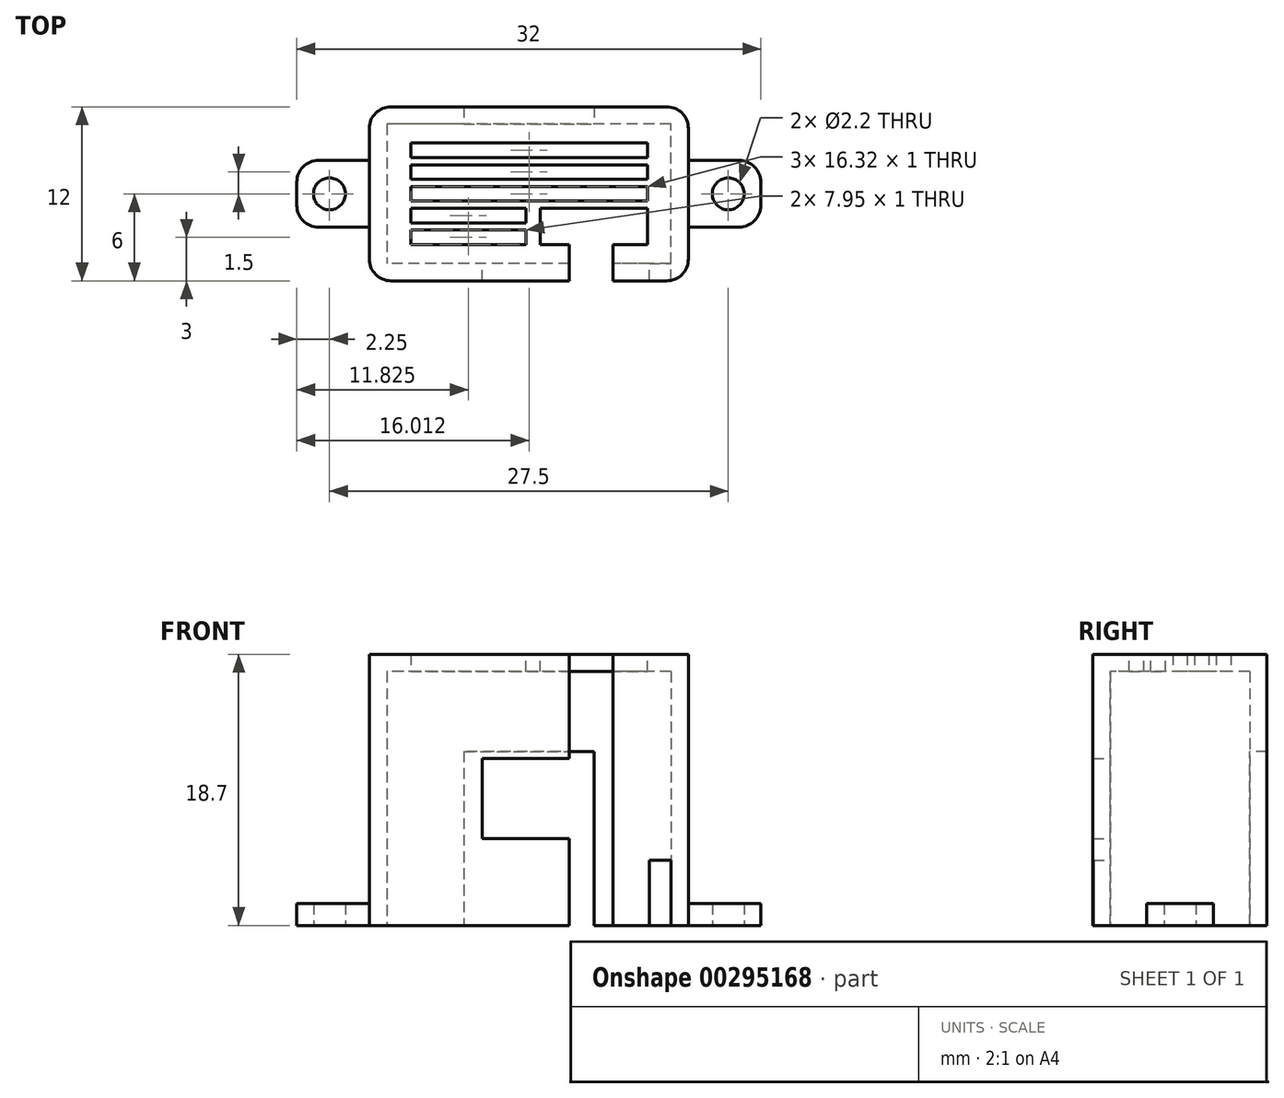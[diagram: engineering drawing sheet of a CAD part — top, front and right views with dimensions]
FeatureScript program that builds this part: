
annotation { "Feature Type Name" : "Feature", "Feature Type Description" : "" }
export const myFeature = defineFeature(function(context is Context, id is Id, definition is map)
    precondition{}
    {
        {
            var Q0;
            Q0=qCreatedBy(makeId("Top.planeOp"),FACE);
            var sketch = newSketch(context, id + "F0", { "sketchPlane" : qUnion([Q0])});
            skLineSegment(sketch, "E0.bottom", {"start": v(1.5, 0) * mm, "end": v(20.5, 0) * mm});
            skLineSegment(sketch, "E0.top", {"start": v(1.5, -12) * mm, "end": v(20.5, -12) * mm});
            skLineSegment(sketch, "E0.left", {"start": v(0, -1.5) * mm, "end": v(0, -10.5) * mm});
            skLineSegment(sketch, "E0.right", {"start": v(22, -1.5) * mm, "end": v(22, -10.5) * mm});
            skLineSegment(sketch, "E1.bottom", {"start": v(0, -3.7) * mm, "end": v(-3.5, -3.7) * mm});
            skLineSegment(sketch, "E1.top", {"start": v(0, -8.3) * mm, "end": v(-3.5, -8.3) * mm});
            skLineSegment(sketch, "E1.left", {"start": v(0, -3.7) * mm, "end": v(0, -8.3) * mm});
            skLineSegment(sketch, "E1.right", {"start": v(-5, -5.2) * mm, "end": v(-5, -6.8) * mm});
            skLineSegment(sketch, "E2.bottom", {"start": v(22, -3.7) * mm, "end": v(25.5, -3.7) * mm});
            skLineSegment(sketch, "E2.top", {"start": v(22, -8.3) * mm, "end": v(25.5, -8.3) * mm});
            skLineSegment(sketch, "E2.left", {"start": v(22, -3.7) * mm, "end": v(22, -8.3) * mm});
            skLineSegment(sketch, "E2.right", {"start": v(27, -5.2) * mm, "end": v(27, -6.8) * mm});
            skLineSegment(sketch, "E3", {"start": v(5.98, -6) * mm, "end": v(14.86, -6) * mm, "construction": true});
            skPoint(sketch, "E3.startSnap0", {"position": v(0, -6) * mm});
            skCircle(sketch, "E4", {"center": v(-2.75, -6) * mm, "radius": 1.1 * mm});
            skCircle(sketch, "E5", {"center": v(24.75, -6) * mm, "radius": 1.1 * mm});
            skPoint(sketch, "E6.visualSharp", {"position": v(-5, -3.7) * mm});
            skArc(sketch, "E7.filletArc", {"start": v(-3.5, -3.7) * mm, "mid": v(-4.56, -4.14) * mm, "end": v(-5, -5.2) * mm});
            skPoint(sketch, "E8.visualSharp", {"position": v(-5, -8.3) * mm});
            skArc(sketch, "E8.filletArc", {"start": v(-5, -6.8) * mm, "mid": v(-4.56, -7.86) * mm, "end": v(-3.5, -8.3) * mm});
            skPoint(sketch, "E9.visualSharp", {"position": v(27, -3.7) * mm});
            skArc(sketch, "E9.filletArc", {"start": v(27, -5.2) * mm, "mid": v(26.56, -4.14) * mm, "end": v(25.5, -3.7) * mm});
            skPoint(sketch, "E10.visualSharp", {"position": v(27, -8.3) * mm});
            skArc(sketch, "E10.filletArc", {"start": v(25.5, -8.3) * mm, "mid": v(26.56, -7.86) * mm, "end": v(27, -6.8) * mm});
            skPoint(sketch, "E11.visualSharp", {"position": v(0, 0) * mm});
            skArc(sketch, "E11.filletArc", {"start": v(1.5, 0) * mm, "mid": v(0.44, -0.44) * mm, "end": v(0, -1.5) * mm});
            skPoint(sketch, "E12.visualSharp", {"position": v(22, 0) * mm});
            skArc(sketch, "E12.filletArc", {"start": v(22, -1.5) * mm, "mid": v(21.56, -0.44) * mm, "end": v(20.5, 0) * mm});
            skPoint(sketch, "E13.visualSharp", {"position": v(22, -12) * mm});
            skArc(sketch, "E13.filletArc", {"start": v(20.5, -12) * mm, "mid": v(21.56, -11.56) * mm, "end": v(22, -10.5) * mm});
            skPoint(sketch, "E14.visualSharp", {"position": v(0, -12) * mm});
            skArc(sketch, "E14.filletArc", {"start": v(0, -10.5) * mm, "mid": v(0.44, -11.56) * mm, "end": v(1.5, -12) * mm});
            skLineSegment(sketch, "E15.0", {"start": v(20.8, -1.5) * mm, "end": v(20.8, -10.5) * mm});
            skLineSegment(sketch, "E15.2", {"start": v(1.5, -1.2) * mm, "end": v(20.5, -1.2) * mm});
            skLineSegment(sketch, "E15.3", {"start": v(1.5, -10.8) * mm, "end": v(20.5, -10.8) * mm});
            skLineSegment(sketch, "E15.5", {"start": v(1.2, -1.5) * mm, "end": v(1.2, -10.5) * mm});
            skLineSegment(sketch, "E16", {"start": v(20.8, -10.5) * mm, "end": v(20.8, -10.8) * mm});
            skLineSegment(sketch, "E17", {"start": v(20.8, -10.8) * mm, "end": v(20.5, -10.8) * mm});
            skLineSegment(sketch, "E18", {"start": v(20.8, -1.5) * mm, "end": v(20.8, -1.2) * mm});
            skLineSegment(sketch, "E19", {"start": v(20.8, -1.2) * mm, "end": v(20.5, -1.2) * mm});
            skLineSegment(sketch, "E20", {"start": v(1.5, -1.2) * mm, "end": v(1.2, -1.2) * mm});
            skLineSegment(sketch, "E21", {"start": v(1.2, -1.2) * mm, "end": v(1.2, -1.5) * mm});
            skLineSegment(sketch, "E22", {"start": v(1.2, -10.5) * mm, "end": v(1.2, -10.8) * mm});
            skLineSegment(sketch, "E23", {"start": v(1.2, -10.8) * mm, "end": v(1.5, -10.8) * mm});
            skSolve(sketch);
        }
        {
            var Q0;
            Q0=makeQuery(id+"F0.imprint","IMPRINT",FACE,{"disambiguationData":[TD([[makeQuery(id+"F0.imprint","IMPRINT",EDGE,{"derivedFrom":sQuery(id+"F0.wireOp",EDGE,"E0.bottom")}),-1.0]])]});
            var Q1;
            Q1=makeQuery(id+"F0.imprint","IMPRINT",FACE,{"disambiguationData":[TD([[makeQuery(id+"F0.imprint","IMPRINT",EDGE,{"derivedFrom":sQuery(id+"F0.wireOp",EDGE,"E1.bottom")}),1.0]])]});
            var Q2;
            Q2=makeQuery(id+"F0.imprint","IMPRINT",FACE,{"disambiguationData":[TD([[makeQuery(id+"F0.imprint","IMPRINT",EDGE,{"derivedFrom":sQuery(id+"F0.wireOp",EDGE,"E2.bottom")}),-1.0]])]});
            var Q3;
            {var subQ0=sQuery(id+"F0.wireOp",EDGE,"jaEvkIbK-e3yD-Nrfl-q2IN-t7q462HMhGoy");Q3=makeQuery(id+"F0.imprint","IMPRINT",FACE,{"disambiguationData":[TD([[makeQuery(id+"F0.imprint","IMPRINT",EDGE,{"derivedFrom":subQ0}),1.0]])]});}
            extrude(context, id + "F1", {"entities" : qUnion([Q0, Q1, Q2, Q3]), "depth" : 1.5 * mm});
        }
        {
            var Q0;
            Q0=makeQuery(id+"F1.opExtrude","CAP_FACE",FACE,{"disambiguationData":[OSD([sQuery(id+"F0.wireOp",EDGE,"E0.bottom"),sQuery(id+"F0.wireOp",EDGE,"E0.top"),sQuery(id+"F0.wireOp",EDGE,"E0.left"),sQuery(id+"F0.wireOp",EDGE,"E0.right"),sQuery(id+"F0.wireOp",EDGE,"E1.bottom"),sQuery(id+"F0.wireOp",EDGE,"E1.top"),sQuery(id+"F0.wireOp",EDGE,"E1.right"),sQuery(id+"F0.wireOp",EDGE,"E2.bottom"),sQuery(id+"F0.wireOp",EDGE,"E2.top"),sQuery(id+"F0.wireOp",EDGE,"E2.right"),sQuery(id+"F0.wireOp",EDGE,"E4"),sQuery(id+"F0.wireOp",EDGE,"E5"),sQuery(id+"F0.wireOp",EDGE,"E7.filletArc"),sQuery(id+"F0.wireOp",EDGE,"E8.filletArc"),sQuery(id+"F0.wireOp",EDGE,"E9.filletArc"),sQuery(id+"F0.wireOp",EDGE,"E10.filletArc"),sQuery(id+"F0.wireOp",EDGE,"E11.filletArc"),sQuery(id+"F0.wireOp",EDGE,"E12.filletArc"),sQuery(id+"F0.wireOp",EDGE,"E13.filletArc"),sQuery(id+"F0.wireOp",EDGE,"E14.filletArc"),sQuery(id+"F0.wireOp",EDGE,"E15.0"),sQuery(id+"F0.wireOp",EDGE,"E15.2"),sQuery(id+"F0.wireOp",EDGE,"E15.3"),sQuery(id+"F0.wireOp",EDGE,"E15.5"),sQuery(id+"F0.wireOp",EDGE,"E16"),sQuery(id+"F0.wireOp",EDGE,"E17"),sQuery(id+"F0.wireOp",EDGE,"E18"),sQuery(id+"F0.wireOp",EDGE,"E19"),sQuery(id+"F0.wireOp",EDGE,"E20"),sQuery(id+"F0.wireOp",EDGE,"E21"),sQuery(id+"F0.wireOp",EDGE,"E22"),sQuery(id+"F0.wireOp",EDGE,"E23")])],"isStart":false});
            var sketch = newSketch(context, id + "F2", { "sketchPlane" : qUnion([Q0])});
            skLineSegment(sketch, "E24", {"start": v(22, -8.3) * mm, "end": v(22, -3.7) * mm});
            skLineSegment(sketch, "E25", {"start": v(0, -8.3) * mm, "end": v(0, -3.7) * mm});
            skSolve(sketch);
        }
        {
            var Q0;
            Q0=makeQuery(id+"F2.imprint","IMPRINT",FACE,{"disambiguationData":[TD([[makeQuery(id+"F2.imprint","IMPRINT",EDGE,{"derivedFrom":sQuery(id+"F2.wireOp",EDGE,"E24")}),1.0]])]});
            extrude(context, id + "F3", {"entities" : qUnion([Q0]), "operationType" : NewBodyOperationType.ADD, "depth" : 16 * mm});
        }
        {
            var Q0;
            {var subQ0=sQuery(id+"F0.wireOp",EDGE,"E23");var subQ1=sQuery(id+"F0.wireOp",EDGE,"E17");var subQ2=sQuery(id+"F0.wireOp",EDGE,"E15.3");Q0=makeQuery(id+"F3.boolean.opBoolean","MERGE",FACE,{"derivedFrom":[makeQuery(id+"F1.opExtrude","SWEPT_FACE",FACE,{"disambiguationData":[OSD([subQ2,subQ1,subQ0])]}),makeQuery(id+"F3.opExtrude","SWEPT_FACE",FACE,{"disambiguationData":[OSD([subQ2,subQ1,subQ0])]})]});}
            var sketch = newSketch(context, id + "F4", { "sketchPlane" : qUnion([Q0])});
            skLineSegment(sketch, "E26", {"start": v(-16.8, 0) * mm, "end": v(-16.8, 17.5) * mm});
            skLineSegment(sketch, "E27", {"start": v(-16.8, 17.5) * mm, "end": v(-13.8, 17.5) * mm});
            skLineSegment(sketch, "E28", {"start": v(-13.8, 17.5) * mm, "end": v(-13.8, 0) * mm});
            skLineSegment(sketch, "E29", {"start": v(-19.3, 0) * mm, "end": v(-19.3, 4.5) * mm});
            skLineSegment(sketch, "E30", {"start": v(-19.3, 4.5) * mm, "end": v(-20.8, 4.5) * mm});
            skLineSegment(sketch, "E31.bottom", {"start": v(-13.8, 6) * mm, "end": v(-7.8, 6) * mm});
            skLineSegment(sketch, "E31.top", {"start": v(-13.8, 11.5) * mm, "end": v(-7.8, 11.5) * mm});
            skLineSegment(sketch, "E31.left", {"start": v(-13.8, 6) * mm, "end": v(-13.8, 11.5) * mm});
            skLineSegment(sketch, "E31.right", {"start": v(-7.8, 6) * mm, "end": v(-7.8, 11.5) * mm});
            skSolve(sketch);
        }
        {
            var Q0;
            {var subQ0=sQuery(id+"F4.wireOp",EDGE,"E29");Q0=makeQuery(id+"F4.imprint","IMPRINT",FACE,{"disambiguationData":[TD([[makeQuery(id+"F4.imprint","IMPRINT",EDGE,{"derivedFrom":subQ0}),1.0]])]});}
            var Q1;
            {var subQ0=sQuery(id+"F4.wireOp",EDGE,"E26");Q1=makeQuery(id+"F4.imprint","IMPRINT",FACE,{"disambiguationData":[TD([[makeQuery(id+"F4.imprint","IMPRINT",EDGE,{"derivedFrom":subQ0}),-1.0]])]});}
            var Q2;
            Q2=makeQuery(id+"F4.imprint","IMPRINT",FACE,{"disambiguationData":[TD([[makeQuery(id+"F4.imprint","IMPRINT",EDGE,{"derivedFrom":sQuery(id+"F4.wireOp",EDGE,"E31.bottom")}),1.0]])]});
            extrude(context, id + "F5", {"entities" : qUnion([Q0, Q1, Q2]), "operationType" : NewBodyOperationType.REMOVE, "oppositeDirection" : true, "depth" : 1.2 * mm});
        }
        {
            var Q0;
            {var subQ0=sQuery(id+"F0.wireOp",EDGE,"E20");var subQ1=sQuery(id+"F0.wireOp",EDGE,"E19");var subQ2=sQuery(id+"F0.wireOp",EDGE,"E15.2");Q0=makeQuery(id+"F3.boolean.opBoolean","MERGE",FACE,{"derivedFrom":[makeQuery(id+"F1.opExtrude","SWEPT_FACE",FACE,{"disambiguationData":[OSD([subQ2,subQ1,subQ0])]}),makeQuery(id+"F3.opExtrude","SWEPT_FACE",FACE,{"disambiguationData":[OSD([subQ2,subQ1,subQ0])]})]});}
            var sketch = newSketch(context, id + "F6", { "sketchPlane" : qUnion([Q0])});
            skLineSegment(sketch, "E32.bottom", {"start": v(6.5, 0) * mm, "end": v(15.5, 0) * mm});
            skLineSegment(sketch, "E32.top", {"start": v(6.5, 12) * mm, "end": v(15.5, 12) * mm});
            skLineSegment(sketch, "E32.left", {"start": v(6.5, 0) * mm, "end": v(6.5, 12) * mm});
            skLineSegment(sketch, "E32.right", {"start": v(15.5, 0) * mm, "end": v(15.5, 12) * mm});
            skSolve(sketch);
        }
        {
            var Q0;
            Q0=makeQuery(id+"F6.imprint","IMPRINT",FACE,{"disambiguationData":[TD([[makeQuery(id+"F6.imprint","IMPRINT",EDGE,{"derivedFrom":sQuery(id+"F6.wireOp",EDGE,"E32.bottom")}),-1.0]])]});
            extrude(context, id + "F7", {"entities" : qUnion([Q0]), "operationType" : NewBodyOperationType.REMOVE, "oppositeDirection" : true, "depth" : 25 * mm});
        }
        {
            var Q0;
            Q0=makeQuery(id+"F3.opExtrude","CAP_FACE",FACE,{"disambiguationData":[OSD([sQuery(id+"F0.wireOp",EDGE,"E0.bottom"),sQuery(id+"F0.wireOp",EDGE,"E0.top"),sQuery(id+"F0.wireOp",EDGE,"E0.left"),sQuery(id+"F0.wireOp",EDGE,"E0.right"),sQuery(id+"F0.wireOp",EDGE,"E11.filletArc"),sQuery(id+"F0.wireOp",EDGE,"E12.filletArc"),sQuery(id+"F0.wireOp",EDGE,"E13.filletArc"),sQuery(id+"F0.wireOp",EDGE,"E14.filletArc"),sQuery(id+"F0.wireOp",EDGE,"E15.0"),sQuery(id+"F0.wireOp",EDGE,"E15.2"),sQuery(id+"F0.wireOp",EDGE,"E15.3"),sQuery(id+"F0.wireOp",EDGE,"E15.5"),sQuery(id+"F0.wireOp",EDGE,"E16"),sQuery(id+"F0.wireOp",EDGE,"E17"),sQuery(id+"F0.wireOp",EDGE,"E18"),sQuery(id+"F0.wireOp",EDGE,"E19"),sQuery(id+"F0.wireOp",EDGE,"E20"),sQuery(id+"F0.wireOp",EDGE,"E21"),sQuery(id+"F0.wireOp",EDGE,"E22"),sQuery(id+"F0.wireOp",EDGE,"E23"),sQuery(id+"F2.wireOp",EDGE,"E24"),sQuery(id+"F2.wireOp",EDGE,"E25")])],"isStart":false});
            var sketch = newSketch(context, id + "F8", { "sketchPlane" : qUnion([Q0])});
            skLineSegment(sketch, "E33", {"start": v(16.8, -12) * mm, "end": v(13.8, -12) * mm});
            skLineSegment(sketch, "E34", {"start": v(4.97, -6) * mm, "end": v(16.54, -6) * mm, "construction": true});
            skPoint(sketch, "E34.startSnap0", {"position": v(1.2, -6) * mm});
            skLineSegment(sketch, "E35.bottom", {"start": v(2.85, -2.5) * mm, "end": v(19.17, -2.5) * mm});
            skLineSegment(sketch, "E35.top", {"start": v(2.85, -3.5) * mm, "end": v(19.17, -3.5) * mm});
            skLineSegment(sketch, "E35.left", {"start": v(2.85, -2.5) * mm, "end": v(2.85, -3.5) * mm});
            skLineSegment(sketch, "E35.right", {"start": v(19.17, -2.5) * mm, "end": v(19.17, -3.5) * mm});
            skLineSegment(sketch, "E36.bottom", {"start": v(2.85, -4) * mm, "end": v(19.17, -4) * mm});
            skLineSegment(sketch, "E36.top", {"start": v(2.85, -5) * mm, "end": v(19.17, -5) * mm});
            skLineSegment(sketch, "E36.left", {"start": v(2.85, -4) * mm, "end": v(2.85, -5) * mm});
            skLineSegment(sketch, "E36.right", {"start": v(19.17, -4) * mm, "end": v(19.17, -5) * mm});
            skPoint(sketch, "E37.firstSnap0", {"position": v(2.85, -4.5) * mm});
            skLineSegment(sketch, "E37.bottom", {"start": v(2.85, -5.5) * mm, "end": v(19.17, -5.5) * mm});
            skLineSegment(sketch, "E37.top", {"start": v(2.85, -6.5) * mm, "end": v(19.17, -6.5) * mm});
            skLineSegment(sketch, "E37.left", {"start": v(2.85, -5.5) * mm, "end": v(2.85, -6.5) * mm});
            skLineSegment(sketch, "E37.right", {"start": v(19.17, -5.5) * mm, "end": v(19.17, -6.5) * mm});
            skLineSegment(sketch, "E38.MirrorCS", {"start": v(2.85, -7) * mm, "end": v(19.17, -7) * mm});
            skLineSegment(sketch, "E39.MirrorCS", {"start": v(2.85, -9.5) * mm, "end": v(2.85, -8.5) * mm});
            skLineSegment(sketch, "E40.MirrorCS", {"start": v(2.85, -9.5) * mm, "end": v(19.17, -9.5) * mm});
            skLineSegment(sketch, "E41.MirrorCS", {"start": v(2.85, -8) * mm, "end": v(19.17, -8) * mm});
            skLineSegment(sketch, "E42.MirrorCS", {"start": v(19.17, -8) * mm, "end": v(19.17, -7) * mm});
            skPoint(sketch, "E43.MirrorP", {"position": v(2.85, -7.5) * mm});
            skLineSegment(sketch, "E44.MirrorCS", {"start": v(2.85, -8.5) * mm, "end": v(19.17, -8.5) * mm});
            skLineSegment(sketch, "E45.MirrorCS", {"start": v(2.85, -8) * mm, "end": v(2.85, -7) * mm});
            skLineSegment(sketch, "E46.MirrorCS", {"start": v(19.17, -9.5) * mm, "end": v(19.17, -8.5) * mm});
            skSolve(sketch);
        }
        {
            var Q0;
            {var subQ16=sQuery(id+"F0.wireOp",EDGE,"E0.bottom");Q0=makeQuery(id+"F8.imprint","IMPRINT",FACE,{"disambiguationData":[TD([[makeQuery(id+"F8.imprint","IMPRINT",EDGE,{"derivedFrom":makeQuery(id+"F3.opExtrude","CAP_EDGE",EDGE,{"disambiguationData":[OSD([subQ16])],"isStart":false})}),-1.0]])]});}
            var Q1;
            Q1=makeQuery(id+"F8.imprint","IMPRINT",FACE,{"disambiguationData":[TD([[makeQuery(id+"F8.imprint","IMPRINT",EDGE,{"derivedFrom":sQuery(id+"F8.wireOp",EDGE,"E33")}),-1.0]])]});
            extrude(context, id + "F9", {"entities" : qUnion([Q0, Q1]), "operationType" : NewBodyOperationType.ADD, "depth" : 1.2 * mm});
        }
        {
            var Q0;
            {var subQ0=sQuery(id+"F0.wireOp",EDGE,"E0.top");var subQ13=sQuery(id+"F0.wireOp",EDGE,"E14.filletArc");var subQ14=sQuery(id+"F0.wireOp",EDGE,"E13.filletArc");var subQ22=makeQuery(id+"F3.boolean.opBoolean","MERGE",FACE,{"derivedFrom":[makeQuery(id+"F1.opExtrude","SWEPT_FACE",FACE,{"disambiguationData":[OSD([subQ0])]}),makeQuery(id+"F3.opExtrude","SWEPT_FACE",FACE,{"disambiguationData":[OSD([subQ0])]})]});Q0=makeQuery(id+"F9.boolean.opBoolean","MERGE",FACE,{"derivedFrom":[makeQuery(id+"F5.boolean.opBoolean","SPLIT",FACE,{"disambiguationData":[TD([makeQuery(id+"F1.opExtrude","SWEPT_FACE",FACE,{"disambiguationData":[OSD([subQ13])]})])],"derivedFrom":subQ22}),makeQuery(id+"F5.boolean.opBoolean","SPLIT",FACE,{"disambiguationData":[TD([makeQuery(id+"F1.opExtrude","SWEPT_FACE",FACE,{"disambiguationData":[OSD([subQ14])]})])],"derivedFrom":subQ22}),makeQuery(id+"F9.opExtrude","SWEPT_FACE",FACE,{"disambiguationData":[OSD([subQ0,sQuery(id+"F8.wireOp",EDGE,"E33")])]})]});}
            var sketch = newSketch(context, id + "F10", { "sketchPlane" : qUnion([Q0])});
            skLineSegment(sketch, "E47", {"start": v(13.8, 17.5) * mm, "end": v(13.8, 18.7) * mm});
            skLineSegment(sketch, "E48", {"start": v(16.8, 17.5) * mm, "end": v(16.8, 18.7) * mm});
            skSolve(sketch);
        }
        {
            var Q0;
            {var subQ0=sQuery(id+"F10.wireOp",EDGE,"E47");Q0=makeQuery(id+"F10.imprint","IMPRINT",FACE,{"disambiguationData":[TD([[makeQuery(id+"F10.imprint","IMPRINT",EDGE,{"derivedFrom":subQ0}),-1.0]])]});}
            extrude(context, id + "F11", {"entities" : qUnion([Q0]), "operationType" : NewBodyOperationType.REMOVE, "oppositeDirection" : true, "depth" : 4 * mm});
        }
        {
            var Q0;
            Q0=makeQuery(id+"F9.opExtrude","CAP_FACE",FACE,{"disambiguationData":[OSD([sQuery(id+"F0.wireOp",EDGE,"E0.bottom"),sQuery(id+"F0.wireOp",EDGE,"E0.top"),sQuery(id+"F0.wireOp",EDGE,"E0.left"),sQuery(id+"F0.wireOp",EDGE,"E0.right"),sQuery(id+"F0.wireOp",EDGE,"E11.filletArc"),sQuery(id+"F0.wireOp",EDGE,"E12.filletArc"),sQuery(id+"F0.wireOp",EDGE,"E13.filletArc"),sQuery(id+"F0.wireOp",EDGE,"E14.filletArc"),sQuery(id+"F2.wireOp",EDGE,"E24"),sQuery(id+"F2.wireOp",EDGE,"E25"),sQuery(id+"F8.wireOp",EDGE,"E33"),sQuery(id+"F8.wireOp",EDGE,"E35.bottom"),sQuery(id+"F8.wireOp",EDGE,"E35.top"),sQuery(id+"F8.wireOp",EDGE,"E35.left"),sQuery(id+"F8.wireOp",EDGE,"E35.right"),sQuery(id+"F8.wireOp",EDGE,"E36.bottom"),sQuery(id+"F8.wireOp",EDGE,"E36.top"),sQuery(id+"F8.wireOp",EDGE,"E36.left"),sQuery(id+"F8.wireOp",EDGE,"E36.right"),sQuery(id+"F8.wireOp",EDGE,"E37.bottom"),sQuery(id+"F8.wireOp",EDGE,"E37.top"),sQuery(id+"F8.wireOp",EDGE,"E37.left"),sQuery(id+"F8.wireOp",EDGE,"E37.right"),sQuery(id+"F8.wireOp",EDGE,"E38.MirrorCS"),sQuery(id+"F8.wireOp",EDGE,"E39.MirrorCS"),sQuery(id+"F8.wireOp",EDGE,"E40.MirrorCS"),sQuery(id+"F8.wireOp",EDGE,"E41.MirrorCS"),sQuery(id+"F8.wireOp",EDGE,"E42.MirrorCS"),sQuery(id+"F8.wireOp",EDGE,"E44.MirrorCS"),sQuery(id+"F8.wireOp",EDGE,"E45.MirrorCS"),sQuery(id+"F8.wireOp",EDGE,"E46.MirrorCS")])],"isStart":false});
            var sketch = newSketch(context, id + "F12", { "sketchPlane" : qUnion([Q0])});
            skLineSegment(sketch, "E49", {"start": v(13.8, -9.5) * mm, "end": v(13.8, -7) * mm});
            skLineSegment(sketch, "E50", {"start": v(10.8, -9.5) * mm, "end": v(10.8, -7) * mm});
            skLineSegment(sketch, "E51", {"start": v(16.8, -9.5) * mm, "end": v(16.8, -7) * mm});
            skLineSegment(sketch, "E52", {"start": v(19.17, -9.5) * mm, "end": v(19.17, -7) * mm});
            skSolve(sketch);
        }
        {
            var Q0;
            {var subQ2=sQuery(id+"F8.wireOp",EDGE,"E44.MirrorCS");var subQ4=sQuery(id+"F8.wireOp",EDGE,"E39.MirrorCS");var subQ10=makeQuery(id+"F9.opExtrude","SWEPT_FACE",FACE,{"disambiguationData":[OSD([subQ4])]});var subQ13=makeQuery(id+"F11.boolean.opBoolean","SPLIT",EDGE,{"disambiguationData":[TD([subQ10])],"derivedFrom":makeQuery(id+"F9.opExtrude","CAP_EDGE",EDGE,{"disambiguationData":[OSD([subQ2])],"isStart":false})});var subQ15=sQuery(id+"F12.wireOp",EDGE,"E50");var subQ17=makeQuery(id+"F12.imprint","INTERSECT",VERTEX,{"derivedFrom":[subQ13,subQ15]});Q0=makeQuery(id+"F12.imprint","IMPRINT",FACE,{"disambiguationData":[TD([[makeQuery(id+"F12.imprint","IMPRINT",EDGE,{"disambiguationData":[TD([[subQ17,1.0]])],"derivedFrom":subQ15}),-1.0]])]});}
            var Q1;
            {var subQ0=sQuery(id+"F12.wireOp",EDGE,"E49");var subQ3=sQuery(id+"F8.wireOp",EDGE,"E38.MirrorCS");var subQ6=makeQuery(id+"F9.opExtrude","CAP_EDGE",EDGE,{"disambiguationData":[OSD([subQ3])],"isStart":false});var subQ7=makeQuery(id+"F12.imprint","INTERSECT",VERTEX,{"derivedFrom":[subQ6,subQ0]});Q1=makeQuery(id+"F12.imprint","IMPRINT",FACE,{"disambiguationData":[TD([[makeQuery(id+"F12.imprint","IMPRINT",EDGE,{"disambiguationData":[TD([[subQ7,1.0]])],"derivedFrom":subQ6}),-1.0]])]});}
            var Q2;
            {var subQ3=sQuery(id+"F8.wireOp",EDGE,"E38.MirrorCS");var subQ5=makeQuery(id+"F9.opExtrude","CAP_EDGE",EDGE,{"disambiguationData":[OSD([subQ3])],"isStart":false});var subQ7=sQuery(id+"F12.wireOp",EDGE,"E52");var subQ8=makeQuery(id+"F12.imprint","INTERSECT",VERTEX,{"derivedFrom":[subQ5,subQ7]});Q2=makeQuery(id+"F12.imprint","IMPRINT",FACE,{"disambiguationData":[TD([[makeQuery(id+"F12.imprint","IMPRINT",EDGE,{"disambiguationData":[TD([[subQ8,1.0]])],"derivedFrom":subQ5}),-1.0]])]});}
            var Q3;
            {var subQ2=sQuery(id+"F8.wireOp",EDGE,"E46.MirrorCS");var subQ3=sQuery(id+"F8.wireOp",EDGE,"E44.MirrorCS");var subQ10=makeQuery(id+"F9.opExtrude","SWEPT_FACE",FACE,{"disambiguationData":[OSD([subQ2])]});var subQ12=makeQuery(id+"F11.boolean.opBoolean","SPLIT",EDGE,{"disambiguationData":[TD([subQ10])],"derivedFrom":makeQuery(id+"F9.opExtrude","CAP_EDGE",EDGE,{"disambiguationData":[OSD([subQ3])],"isStart":false})});Q3=makeQuery(id+"F12.imprint","IMPRINT",FACE,{"disambiguationData":[TD([[makeQuery(id+"F12.imprint","IMPRINT",EDGE,{"derivedFrom":subQ12}),-1.0]])]});}
            extrude(context, id + "F13", {"entities" : qUnion([Q0, Q1, Q2, Q3]), "operationType" : NewBodyOperationType.ADD, "oppositeDirection" : true, "depth" : 1.2 * mm});
        }
        {
            var Q0;
            {var subQ0=sQuery(id+"F12.wireOp",EDGE,"E52");var subQ1=sQuery(id+"F12.wireOp",EDGE,"E51");var subQ2=sQuery(id+"F8.wireOp",EDGE,"E41.MirrorCS");var subQ3=sQuery(id+"F8.wireOp",EDGE,"E38.MirrorCS");var subQ4=sQuery(id+"F8.wireOp",EDGE,"E44.MirrorCS");var subQ5=sQuery(id+"F8.wireOp",EDGE,"E40.MirrorCS");var subQ6=sQuery(id+"F12.wireOp",EDGE,"E50");var subQ7=sQuery(id+"F12.wireOp",EDGE,"E49");Q0=makeQuery(id+"F13.boolean.opBoolean","MERGE",FACE,{"derivedFrom":[makeQuery(id+"F9.opExtrude","CAP_FACE",FACE,{"disambiguationData":[OSD([sQuery(id+"F0.wireOp",EDGE,"E0.bottom"),sQuery(id+"F0.wireOp",EDGE,"E0.top"),sQuery(id+"F0.wireOp",EDGE,"E0.left"),sQuery(id+"F0.wireOp",EDGE,"E0.right"),sQuery(id+"F0.wireOp",EDGE,"E11.filletArc"),sQuery(id+"F0.wireOp",EDGE,"E12.filletArc"),sQuery(id+"F0.wireOp",EDGE,"E13.filletArc"),sQuery(id+"F0.wireOp",EDGE,"E14.filletArc"),sQuery(id+"F2.wireOp",EDGE,"E24"),sQuery(id+"F2.wireOp",EDGE,"E25"),sQuery(id+"F8.wireOp",EDGE,"E33"),sQuery(id+"F8.wireOp",EDGE,"E35.bottom"),sQuery(id+"F8.wireOp",EDGE,"E35.top"),sQuery(id+"F8.wireOp",EDGE,"E35.left"),sQuery(id+"F8.wireOp",EDGE,"E35.right"),sQuery(id+"F8.wireOp",EDGE,"E36.bottom"),sQuery(id+"F8.wireOp",EDGE,"E36.top"),sQuery(id+"F8.wireOp",EDGE,"E36.left"),sQuery(id+"F8.wireOp",EDGE,"E36.right"),sQuery(id+"F8.wireOp",EDGE,"E37.bottom"),sQuery(id+"F8.wireOp",EDGE,"E37.top"),sQuery(id+"F8.wireOp",EDGE,"E37.left"),sQuery(id+"F8.wireOp",EDGE,"E37.right"),subQ3,sQuery(id+"F8.wireOp",EDGE,"E39.MirrorCS"),subQ5,subQ2,sQuery(id+"F8.wireOp",EDGE,"E42.MirrorCS"),subQ4,sQuery(id+"F8.wireOp",EDGE,"E45.MirrorCS"),sQuery(id+"F8.wireOp",EDGE,"E46.MirrorCS")])],"isStart":false}),makeQuery(id+"F13.opExtrude","CAP_FACE",FACE,{"disambiguationData":[OSD([subQ5,subQ4,subQ7,subQ6])],"isStart":true}),makeQuery(id+"F13.opExtrude","CAP_FACE",FACE,{"disambiguationData":[OSD([subQ3,subQ2,subQ7,subQ6])],"isStart":true}),makeQuery(id+"F13.opExtrude","CAP_FACE",FACE,{"disambiguationData":[OSD([subQ5,subQ4,subQ1,subQ0])],"isStart":true}),makeQuery(id+"F13.opExtrude","CAP_FACE",FACE,{"disambiguationData":[OSD([subQ3,subQ2,subQ1,subQ0])],"isStart":true})]});}
            var sketch = newSketch(context, id + "F14", { "sketchPlane" : qUnion([Q0])});
            skLineSegment(sketch, "E53", {"start": v(19.17, -7) * mm, "end": v(19.17, -9.5) * mm});
            skLineSegment(sketch, "E54", {"start": v(19.17, -9.5) * mm, "end": v(11.8, -9.5) * mm});
            skLineSegment(sketch, "E55", {"start": v(11.8, -9.5) * mm, "end": v(11.8, -7) * mm});
            skLineSegment(sketch, "E56", {"start": v(11.8, -7) * mm, "end": v(19.17, -7) * mm});
            skSolve(sketch);
        }
        {
            var Q0;
            {var subQ0=sQuery(id+"F14.wireOp",EDGE,"E55");Q0=makeQuery(id+"F14.imprint","IMPRINT",FACE,{"disambiguationData":[TD([[makeQuery(id+"F14.imprint","IMPRINT",EDGE,{"derivedFrom":subQ0}),-1.0]])]});}
            var Q1;
            {var subQ0=sQuery(id+"F14.wireOp",EDGE,"E53");Q1=makeQuery(id+"F14.imprint","IMPRINT",FACE,{"disambiguationData":[TD([[makeQuery(id+"F14.imprint","IMPRINT",EDGE,{"derivedFrom":subQ0}),-1.0]])]});}
            extrude(context, id + "F15", {"entities" : qUnion([Q0, Q1]), "operationType" : NewBodyOperationType.REMOVE, "oppositeDirection" : true, "depth" : 1.2 * mm});
        }
    });
